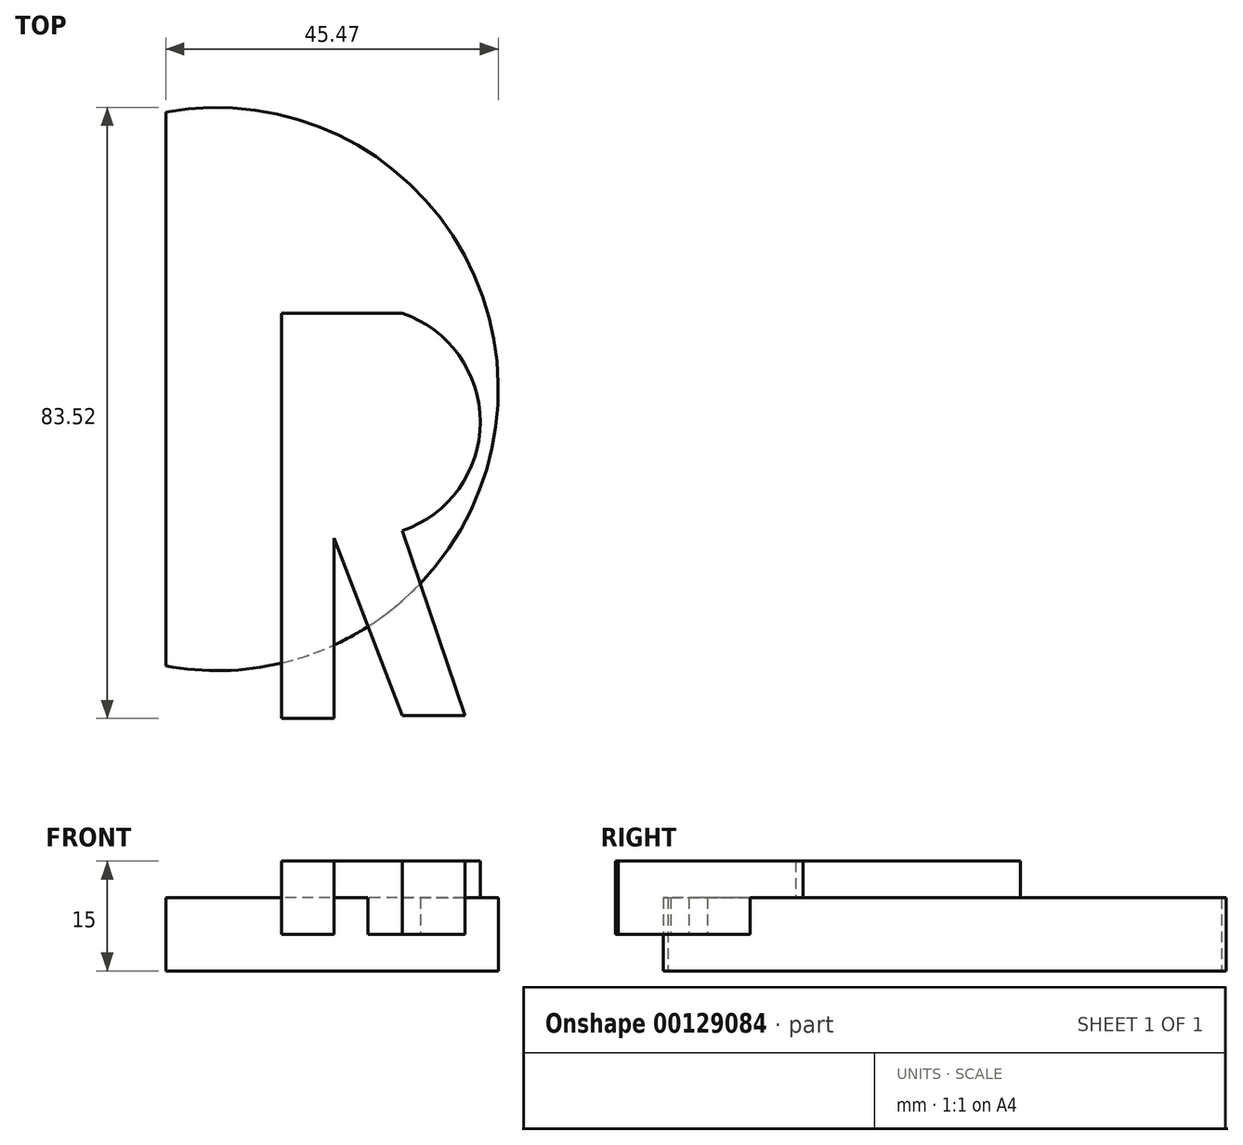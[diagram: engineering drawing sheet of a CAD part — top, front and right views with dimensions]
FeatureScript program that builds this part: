
annotation { "Feature Type Name" : "Feature", "Feature Type Description" : "" }
export const myFeature = defineFeature(function(context is Context, id is Id, definition is map)
    precondition{}
    {
        {
            var Q0;
            Q0=qCreatedBy(makeId("Top.planeOp"),FACE);
            var sketch = newSketch(context, id + "F0", { "sketchPlane" : qUnion([Q0])});
            skLineSegment(sketch, "E0", {"start": v(-32.37, 40.77) * mm, "end": v(-32.37, -34.93) * mm});
            skArc(sketch, "E1", {"start": v(-32.37, -34.93) * mm, "mid": v(13.1, 2.92) * mm, "end": v(-32.37, 40.77) * mm});
            skSolve(sketch);
        }
        {
            var Q0;
            Q0 = qSketchRegion(id + "F0", true);
            extrude(context, id + "F1", {"entities" : qUnion([Q0]), "depth" : 10 * mm});
        }
        {
            var Q0;
            Q0=makeQuery(id+"F1.opExtrude","CAP_FACE",FACE,{"disambiguationData":[OSD([sQuery(id+"F0.wireOp",EDGE,"E0"),sQuery(id+"F0.wireOp",EDGE,"E1")])],"isStart":false});
            var sketch = newSketch(context, id + "F2", { "sketchPlane" : qUnion([Q0])});
            skLineSegment(sketch, "E2", {"start": v(-16.53, 13.26) * mm, "end": v(-16.53, -42.11) * mm});
            skLineSegment(sketch, "E3", {"start": v(-16.53, -42.11) * mm, "end": v(-9.37, -42.11) * mm});
            skLineSegment(sketch, "E4", {"start": v(-9.37, -42.11) * mm, "end": v(-9.37, -17.48) * mm});
            skLineSegment(sketch, "E5", {"start": v(-9.37, -17.48) * mm, "end": v(0, -41.69) * mm});
            skLineSegment(sketch, "E6", {"start": v(0, -41.69) * mm, "end": v(8.53, -41.69) * mm});
            skLineSegment(sketch, "E7", {"start": v(8.53, -41.69) * mm, "end": v(0, -16.42) * mm});
            skLineSegment(sketch, "E8", {"start": v(-16.53, 13.26) * mm, "end": v(0, 13.26) * mm});
            skArc(sketch, "E9", {"start": v(0, -16.42) * mm, "mid": v(10.64, -1.58) * mm, "end": v(0, 13.26) * mm});
            skSolve(sketch);
        }
        {
            var Q0;
            Q0 = qSketchRegion(id + "F2", true);
            extrude(context, id + "F3", {"entities" : qUnion([Q0]), "operationType" : NewBodyOperationType.ADD, "endBound" : BoundingType.SYMMETRIC, "depth" : 10 * mm});
        }
    });
